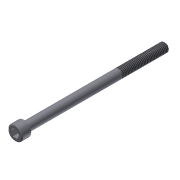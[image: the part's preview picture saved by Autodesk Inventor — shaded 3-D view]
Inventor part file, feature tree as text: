
AUTODESK INVENTOR PART (.ipt)
format: ipt  version: 2011 (Build 150239000, 239)  size: 94,208 bytes
history: native  units: in
note: dims shown in document units (in); Inventor stores cm internally (conversion verified against a paired STEP export)
features: extrude x3, sketch x3, chamfer x2, thread x1
ambient origin geometry x8: Origin, YZ Plane, XZ Plane, XY Plane, X Axis, Y Axis, Z Axis, Center Point
bodies: Solid1 (feature_tree)
feature tree (9):
  extrude  "Extrusion1"  Depth=0.19in TaperAngle=0.0deg
  extrude  "Extrusion2"  Depth=3.0in TaperAngle=0.0deg
  extrude  "Extrusion3"  Depth=0.125in TaperAngle=0.0deg
  thread  "Thread1"  [1 undecoded]
  chamfer  "Chamfer1"  Distance=0.02in Angle=45.0deg
  chamfer  "Chamfer2"  Distance=0.02in Angle=45.0deg
  sketch  "Sketch1"  dims[d0=0.312in d1=0.19in d2=0.0in]
  sketch  "Sketch2"  dims[d3=0.19in d4=3.0in d5=0.0in]
  sketch  "Sketch3"  dims[d6=0.1562in d7=0.125in d8=0.0in d9=1.0in d10=0.0in d11=0.02in d12=0.125in d13=45.0deg d14=0.02in d15=0.125in d16=45.0deg]
note: 1 required parameter value undecoded (feature->parameter linkage not recoverable at this tier; creation-order binding heuristic only, values carry confidence <= 0.55)
